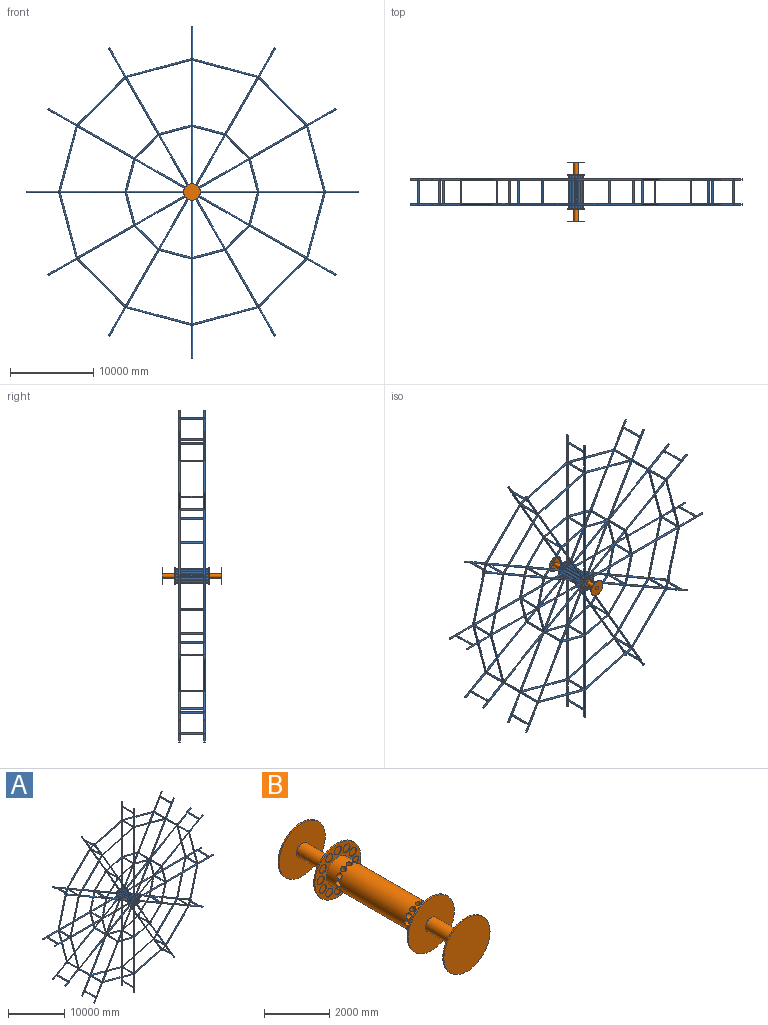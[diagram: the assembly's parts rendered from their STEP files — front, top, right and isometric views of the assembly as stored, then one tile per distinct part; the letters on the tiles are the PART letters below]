
ASSEMBLY  parts=2 mates=1
PART A: 240 faces, bbox 40000x4040x40000 mm
  f0: cylinder r=100mm len=7138.2mm, axis (1,0,0), area 4413707.7mm2, adj f8,f15,f18,f225
  f1: cylinder r=100mm len=8000mm, axis (1,0,0), area 4927074.2mm2, adj f15,f16,f18,f19,f218,f225
  f2: cylinder r=100mm len=638.2mm, axis (1,0,0), area 239270.4mm2, adj f8,f89,f217
  f3: cylinder r=100mm len=8000mm, axis (1,0,0), area 4927074.2mm2, adj f6,f7,f15,f16,f223,f224
  f4: cylinder r=100mm len=7138.2mm, axis (1,0,0), area 4413701.9mm2, adj f6,f8,f15,f224
  f5: cylinder r=100mm len=638.2mm, axis (1,0,0), area 239279.2mm2, adj f8,f95,f216
  f6: cylinder r=100mm len=4051.76mm, axis (-0.26,0,0.97), area 2502458.8mm2, adj f3,f4,f15,f206,f207,f222
  f7: cylinder r=100mm len=8051.76mm, axis (-0.26,0,0.97), area 5104391.6mm2, adj f3,f14,f16,f205,f221,f222
  f8: cylinder r=150mm len=4040mm, axis (0,1,0), area 3673361.7mm2, adj f0,f2,f4,f5,f9,f10
  f9: plane 300x300mm, normal (0,-1,0), area 70685.8mm2, adj f8
  f10: plane 300x300mm, normal (0,1,0), area 70685.8mm2, adj f8
  f11: plane 200x200mm, normal (1,0,0), area 31415.9mm2, adj f12
  f12: cylinder r=100mm len=4000mm, axis (1,0,0), area 2432718.2mm2, adj f11,f16,f17,f19,f218
  f13: plane 200x200mm, normal (1,0,0), area 31415.9mm2, adj f14
  f14: cylinder r=100mm len=4000mm, axis (1,0,0), area 2432718.2mm2, adj f7,f13,f16,f17,f223
  f15: cylinder r=100mm len=2878.25mm, axis (0,1,0), area 1772786.4mm2, adj f0,f1,f3,f4,f6,f18,f224,f225
  f16: cylinder r=100mm len=2878.25mm, axis (0,1,0), area 1772786.4mm2, adj f1,f3,f7,f12,f14,f19,f218,f223
  f17: cylinder r=100mm len=3000mm, axis (0,1,0), area 1804955.6mm2, adj f12,f14
  f18: cylinder r=100mm len=4051.76mm, axis (-0.26,0,0.97), area 2502458.8mm2, adj f0,f1,f15,f206,f209,f220
  f19: cylinder r=100mm len=8051.76mm, axis (-0.26,0,0.97), area 5104391.6mm2, adj f1,f12,f16,f205,f219,f220
  f20: cylinder r=100mm len=652.7mm, axis (0.87,0,0.5), area 239274.4mm2, adj f24,f201,f239
  f21: plane 200x173.21mm, normal (-0.87,0,-0.5), area 31415.9mm2, adj f28
  f22: plane 200x173.21mm, normal (-0.87,0,-0.5), area 31415.9mm2, adj f31
  f23: cylinder r=100mm len=3000mm, axis (0,1,0), area 1804955.6mm2, adj f28,f31
  f24: cylinder r=150mm len=4040mm, axis (0,1,0), area 3673404.8mm2, adj f20,f25,f26,f27,f30,f32
  f25: plane 300x300mm, normal (0,-1,0), area 70685.8mm2, adj f24
  f26: plane 300x300mm, normal (0,1,0), area 70685.8mm2, adj f24
  f27: cylinder r=100mm len=652.7mm, axis (0.87,0,0.5), area 239269.5mm2, adj f24,f194,f234
  f28: cylinder r=100mm len=3564.1mm, axis (0.87,0,0.5), area 2432718.2mm2, adj f21,f23,f107,f128,f130
  f29: cylinder r=100mm len=7028.2mm, axis (0.87,0,0.5), area 4927074.2mm2, adj f106,f107,f128,f129,f130,f131
  f30: cylinder r=100mm len=6281.86mm, axis (0.87,0,0.5), area 4413703.6mm2, adj f24,f106,f129,f131
  f31: cylinder r=100mm len=3564.1mm, axis (0.87,0,0.5), area 2432718.2mm2, adj f22,f23,f103,f130,f132
  f32: cylinder r=100mm len=6281.86mm, axis (0.87,0,0.5), area 4413706.1mm2, adj f24,f102,f131,f133
  f33: cylinder r=100mm len=7028.2mm, axis (0.87,0,0.5), area 4927074.2mm2, adj f102,f103,f130,f131,f132,f133
  f34: cylinder r=100mm len=7028.2mm, axis (0.5,0,0.87), area 4927074.2mm2, adj f40,f41,f49,f50,f214,f215
  f35: cylinder r=100mm len=3564.1mm, axis (0.5,0,0.87), area 2432718.2mm2, adj f41,f47,f50,f51,f214
  f36: cylinder r=100mm len=7028.2mm, axis (0.5,0,0.87), area 4927074.2mm2, adj f49,f50,f52,f53,f202,f203
  f37: cylinder r=100mm len=3564.1mm, axis (0.5,0,0.87), area 2432718.2mm2, adj f45,f50,f51,f53,f202
  f38: cylinder r=100mm len=652.7mm, axis (0.5,0,0.87), area 239270.4mm2, adj f42,f183,f217
  f39: cylinder r=100mm len=652.7mm, axis (0.5,0,0.87), area 239279.2mm2, adj f42,f182,f216
  f40: cylinder r=100mm len=4051.76mm, axis (-0.97,0,0.26), area 2502458.8mm2, adj f34,f48,f49,f172,f173,f187
  f41: cylinder r=100mm len=8051.76mm, axis (-0.97,0,0.26), area 5104391.6mm2, adj f34,f35,f50,f171,f186,f187
  f42: cylinder r=150mm len=4040mm, axis (0,1,0), area 3673361.7mm2, adj f38,f39,f43,f44,f46,f48
  f43: plane 300x300mm, normal (0,-1,0), area 70685.8mm2, adj f42
  f44: plane 300x300mm, normal (0,1,0), area 70685.8mm2, adj f42
  f45: plane 200x173.21mm, normal (0.5,0,0.87), area 31415.9mm2, adj f37
  f46: cylinder r=100mm len=6281.86mm, axis (0.5,0,0.87), area 4413707.7mm2, adj f42,f49,f52,f203
  f47: plane 200x173.21mm, normal (0.5,0,0.87), area 31415.9mm2, adj f35
  f48: cylinder r=100mm len=6281.86mm, axis (0.5,0,0.87), area 4413701.9mm2, adj f40,f42,f49,f215
  f49: cylinder r=100mm len=2878.25mm, axis (0,1,0), area 1772786.4mm2, adj f34,f36,f40,f46,f48,f52,f203,f215
  f50: cylinder r=100mm len=2878.25mm, axis (0,1,0), area 1772786.4mm2, adj f34,f35,f36,f37,f41,f53,f202,f214
  f51: cylinder r=100mm len=3000mm, axis (0,1,0), area 1804955.6mm2, adj f35,f37
  f52: cylinder r=100mm len=4051.76mm, axis (-0.97,0,0.26), area 2502458.8mm2, adj f36,f46,f49,f172,f175,f185
  f53: cylinder r=100mm len=8051.76mm, axis (-0.97,0,0.26), area 5104391.6mm2, adj f36,f37,f50,f171,f184,f185
  f54: cylinder r=100mm len=638.2mm, axis (0,0,1), area 239274.4mm2, adj f58,f167,f201
  f55: plane 200x200mm, normal (0,0,-1), area 31415.9mm2, adj f62
  f56: plane 200x200mm, normal (0,0,-1), area 31415.9mm2, adj f65
  f57: cylinder r=100mm len=3000mm, axis (0,1,0), area 1804955.6mm2, adj f62,f65
  f58: cylinder r=150mm len=4040mm, axis (0,1,0), area 3673404.8mm2, adj f54,f59,f60,f61,f64,f66
  f59: plane 300x300mm, normal (0,-1,0), area 70685.8mm2, adj f58
  f60: plane 300x300mm, normal (0,1,0), area 70685.8mm2, adj f58
  f61: cylinder r=100mm len=638.2mm, axis (0,0,1), area 239269.5mm2, adj f58,f160,f194
  f62: cylinder r=100mm len=4000mm, axis (0,0,1), area 2432718.2mm2, adj f55,f57,f113,f122,f124
  f63: cylinder r=100mm len=8000mm, axis (0,0,1), area 4927074.2mm2, adj f112,f113,f122,f123,f124,f125
  f64: cylinder r=100mm len=7138.2mm, axis (0,0,1), area 4413703.6mm2, adj f58,f112,f123,f125
  f65: cylinder r=100mm len=4000mm, axis (0,0,1), area 2432718.2mm2, adj f56,f57,f109,f124,f126
  f66: cylinder r=100mm len=7138.2mm, axis (0,0,1), area 4413706.1mm2, adj f58,f108,f125,f127
  f67: cylinder r=100mm len=8000mm, axis (0,0,1), area 4927074.2mm2, adj f108,f109,f124,f125,f126,f127
  f68: cylinder r=100mm len=7028.2mm, axis (-0.5,0,0.87), area 4927074.2mm2, adj f74,f75,f83,f84,f180,f181
  f69: cylinder r=100mm len=3564.1mm, axis (-0.5,0,0.87), area 2432718.2mm2, adj f75,f81,f84,f85,f180
  f70: cylinder r=100mm len=7028.2mm, axis (-0.5,0,0.87), area 4927074.2mm2, adj f83,f84,f86,f87,f168,f169
  f71: cylinder r=100mm len=3564.1mm, axis (-0.5,0,0.87), area 2432718.2mm2, adj f79,f84,f85,f87,f168
  f72: cylinder r=100mm len=652.7mm, axis (-0.5,0,0.87), area 239270.4mm2, adj f76,f149,f183
  f73: cylinder r=100mm len=652.7mm, axis (-0.5,0,0.87), area 239279.2mm2, adj f76,f148,f182
  f74: cylinder r=100mm len=3069.62mm, axis (-0.71,0,-0.71), area 2502458.8mm2, adj f68,f82,f83,f138,f139,f153
  f75: cylinder r=100mm len=5997.83mm, axis (-0.71,0,-0.71), area 5104391.6mm2, adj f68,f69,f84,f137,f152,f153
  f76: cylinder r=150mm len=4040mm, axis (0,1,0), area 3673361.7mm2, adj f72,f73,f77,f78,f80,f82
  f77: plane 300x300mm, normal (0,-1,0), area 70685.8mm2, adj f76
  f78: plane 300x300mm, normal (0,1,0), area 70685.8mm2, adj f76
  f79: plane 200x173.21mm, normal (-0.5,0,0.87), area 31415.9mm2, adj f71
  f80: cylinder r=100mm len=6281.86mm, axis (-0.5,0,0.87), area 4413707.7mm2, adj f76,f83,f86,f169
  f81: plane 200x173.21mm, normal (-0.5,0,0.87), area 31415.9mm2, adj f69
  f82: cylinder r=100mm len=6281.86mm, axis (-0.5,0,0.87), area 4413701.9mm2, adj f74,f76,f83,f181
  f83: cylinder r=100mm len=2878.25mm, axis (0,1,0), area 1772786.4mm2, adj f68,f70,f74,f80,f82,f86,f169,f181
  f84: cylinder r=100mm len=2878.25mm, axis (0,1,0), area 1772786.4mm2, adj f68,f69,f70,f71,f75,f87,f168,f180
  f85: cylinder r=100mm len=3000mm, axis (0,1,0), area 1804955.6mm2, adj f69,f71
  f86: cylinder r=100mm len=3069.62mm, axis (-0.71,0,-0.71), area 2502458.8mm2, adj f70,f80,f83,f138,f141,f151
  f87: cylinder r=100mm len=5997.83mm, axis (-0.71,0,-0.71), area 5104391.6mm2, adj f70,f71,f84,f137,f150,f151
  f88: plane 200x173.21mm, normal (0.87,0,-0.5), area 31415.9mm2, adj f96
  f89: cylinder r=100mm len=652.69mm, axis (-0.87,0,0.5), area 239271.8mm2, adj f2,f92,f167
  f90: plane 200x173.21mm, normal (0.87,0,-0.5), area 31415.9mm2, adj f99
  f91: cylinder r=100mm len=3000mm, axis (0,1,0), area 1804955.6mm2, adj f96,f99
  f92: cylinder r=150mm len=4040mm, axis (0,1,0), area 3673443.3mm2, adj f89,f93,f94,f95,f98,f100
  f93: plane 300x300mm, normal (0,-1,0), area 70685.8mm2, adj f92
  f94: plane 300x300mm, normal (0,1,0), area 70685.8mm2, adj f92
  f95: cylinder r=100mm len=652.69mm, axis (-0.87,0,0.5), area 239270.8mm2, adj f5,f92,f160
  f96: cylinder r=100mm len=3564.1mm, axis (-0.87,0,0.5), area 2432718.2mm2, adj f88,f91,f119,f120,f218
  f97: cylinder r=100mm len=7028.2mm, axis (-0.87,0,0.5), area 4927074.2mm2, adj f118,f119,f120,f121,f218,f225
  f98: cylinder r=100mm len=6281.86mm, axis (-0.87,0,0.5), area 4413703.6mm2, adj f92,f118,f121,f225
  f99: cylinder r=100mm len=3564.1mm, axis (-0.87,0,0.5), area 2432718.2mm2, adj f90,f91,f115,f120,f223
  f100: cylinder r=100mm len=6281.86mm, axis (-0.87,0,0.5), area 4413706.1mm2, adj f92,f114,f121,f224
  f101: cylinder r=100mm len=7028.2mm, axis (-0.87,0,0.5), area 4927074.2mm2, adj f114,f115,f120,f121,f223,f224
  f102: cylinder r=100mm len=4051.76mm, axis (0.26,0,-0.97), area 2502458.8mm2, adj f32,f33,f104,f131,f226,f227
  f103: cylinder r=100mm len=8051.76mm, axis (0.26,0,-0.97), area 5104391.6mm2, adj f31,f33,f105,f130,f226,f228
  f104: cylinder r=100mm len=2878.25mm, axis (0,1,0), area 1772786.4mm2, adj f102,f106,f135,f147,f226,f227,f229,f230
  f105: cylinder r=100mm len=2878.25mm, axis (0,1,0), area 1772786.4mm2, adj f103,f107,f134,f146,f226,f228,f230,f231
  f106: cylinder r=100mm len=4051.76mm, axis (0.26,0,-0.97), area 2502458.8mm2, adj f29,f30,f104,f131,f229,f230
  f107: cylinder r=100mm len=8051.76mm, axis (0.26,0,-0.97), area 5104391.6mm2, adj f28,f29,f105,f130,f230,f231
  f108: cylinder r=100mm len=4051.76mm, axis (0.97,0,-0.26), area 2502458.8mm2, adj f66,f67,f110,f125,f188,f189
  f109: cylinder r=100mm len=8051.76mm, axis (0.97,0,-0.26), area 5104391.6mm2, adj f65,f67,f111,f124,f188,f190
  f110: cylinder r=100mm len=2878.25mm, axis (0,1,0), area 1772786.4mm2, adj f108,f112,f129,f133,f188,f189,f191,f192
  f111: cylinder r=100mm len=2878.25mm, axis (0,1,0), area 1772786.4mm2, adj f109,f113,f128,f132,f188,f190,f192,f193
  f112: cylinder r=100mm len=4051.76mm, axis (0.97,0,-0.26), area 2502458.8mm2, adj f63,f64,f110,f125,f191,f192
  f113: cylinder r=100mm len=8051.76mm, axis (0.97,0,-0.26), area 5104391.6mm2, adj f62,f63,f111,f124,f192,f193
  f114: cylinder r=100mm len=3069.62mm, axis (0.71,0,0.71), area 2502458.8mm2, adj f100,f101,f116,f121,f154,f155
  f115: cylinder r=100mm len=5997.83mm, axis (0.71,0,0.71), area 5104391.6mm2, adj f99,f101,f117,f120,f154,f156
  f116: cylinder r=100mm len=2878.25mm, axis (0,1,0), area 1772786.4mm2, adj f114,f118,f123,f127,f154,f155,f157,f158
  f117: cylinder r=100mm len=2878.25mm, axis (0,1,0), area 1772786.4mm2, adj f115,f119,f122,f126,f154,f156,f158,f159
  f118: cylinder r=100mm len=3069.62mm, axis (0.71,0,0.71), area 2502458.8mm2, adj f97,f98,f116,f121,f157,f158
  f119: cylinder r=100mm len=5997.83mm, axis (0.71,0,0.71), area 5104391.6mm2, adj f96,f97,f117,f120,f158,f159
  f120: cylinder r=100mm len=2878.25mm, axis (0,1,0), area 1772786.4mm2, adj f96,f97,f99,f101,f115,f119,f218,f223
  f121: cylinder r=100mm len=2878.25mm, axis (0,1,0), area 1772786.4mm2, adj f97,f98,f100,f101,f114,f118,f224,f225
  f122: cylinder r=100mm len=8051.76mm, axis (0.97,0,0.26), area 5104391.6mm2, adj f62,f63,f117,f124,f158,f159
  f123: cylinder r=100mm len=4051.76mm, axis (0.97,0,0.26), area 2502458.8mm2, adj f63,f64,f116,f125,f157,f158
  f124: cylinder r=100mm len=2878.25mm, axis (0,1,0), area 1772786.4mm2, adj f62,f63,f65,f67,f109,f113,f122,f126
  f125: cylinder r=100mm len=2878.25mm, axis (0,1,0), area 1772786.4mm2, adj f63,f64,f66,f67,f108,f112,f123,f127
  f126: cylinder r=100mm len=8051.76mm, axis (0.97,0,0.26), area 5104391.6mm2, adj f65,f67,f117,f124,f154,f156
  f127: cylinder r=100mm len=4051.76mm, axis (0.97,0,0.26), area 2502458.8mm2, adj f66,f67,f116,f125,f154,f155
  f128: cylinder r=100mm len=5997.83mm, axis (0.71,0,-0.71), area 5104391.6mm2, adj f28,f29,f111,f130,f192,f193
  f129: cylinder r=100mm len=3069.62mm, axis (0.71,0,-0.71), area 2502458.8mm2, adj f29,f30,f110,f131,f191,f192
  f130: cylinder r=100mm len=2878.25mm, axis (0,1,0), area 1772786.4mm2, adj f28,f29,f31,f33,f103,f107,f128,f132
  f131: cylinder r=100mm len=2878.25mm, axis (0,1,0), area 1772786.4mm2, adj f29,f30,f32,f33,f102,f106,f129,f133
  f132: cylinder r=100mm len=5997.83mm, axis (0.71,0,-0.71), area 5104391.6mm2, adj f31,f33,f111,f130,f188,f190
  f133: cylinder r=100mm len=3069.62mm, axis (0.71,0,-0.71), area 2502458.8mm2, adj f32,f33,f110,f131,f188,f189
  f134: cylinder r=100mm len=8051.76mm, axis (-0.26,0,-0.97), area 5104391.6mm2, adj f105,f137,f150,f151,f230,f231
  f135: cylinder r=100mm len=4051.76mm, axis (-0.26,0,-0.97), area 2502458.8mm2, adj f104,f138,f141,f151,f229,f230
  f136: cylinder r=100mm len=3000mm, axis (0,1,0), area 1804955.6mm2, adj f150,f152
  f137: cylinder r=100mm len=2878.25mm, axis (0,1,0), area 1772786.4mm2, adj f75,f87,f134,f146,f150,f151,f152,f153
  f138: cylinder r=100mm len=2878.25mm, axis (0,1,0), area 1772786.4mm2, adj f74,f86,f135,f139,f141,f147,f151,f153
  f139: cylinder r=100mm len=6281.86mm, axis (-0.87,0,0.5), area 4413701.9mm2, adj f74,f138,f145,f147
  f140: plane 200x173.21mm, normal (-0.87,0,0.5), area 31415.9mm2, adj f152
  f141: cylinder r=100mm len=6281.86mm, axis (-0.87,0,0.5), area 4413707.7mm2, adj f86,f135,f138,f145
  f142: plane 200x173.21mm, normal (-0.87,0,0.5), area 31415.9mm2, adj f150
  f143: plane 300x300mm, normal (0,1,0), area 70685.8mm2, adj f145
  f144: plane 300x300mm, normal (0,-1,0), area 70685.8mm2, adj f145
  f145: cylinder r=150mm len=4040mm, axis (0,1,0), area 3673361.7mm2, adj f139,f141,f143,f144,f148,f149
  f146: cylinder r=100mm len=8051.76mm, axis (-0.26,0,-0.97), area 5104391.6mm2, adj f105,f137,f152,f153,f226,f228
  f147: cylinder r=100mm len=4051.76mm, axis (-0.26,0,-0.97), area 2502458.8mm2, adj f104,f138,f139,f153,f226,f227
  f148: cylinder r=100mm len=652.7mm, axis (-0.87,0,0.5), area 239279.3mm2, adj f73,f145,f234
  f149: cylinder r=100mm len=652.7mm, axis (-0.87,0,0.5), area 239270.5mm2, adj f72,f145,f239
  f150: cylinder r=100mm len=3564.1mm, axis (-0.87,0,0.5), area 2432718.2mm2, adj f87,f134,f136,f137,f142
  f151: cylinder r=100mm len=7028.2mm, axis (-0.87,0,0.5), area 4927074.2mm2, adj f86,f87,f134,f135,f137,f138
  f152: cylinder r=100mm len=3564.1mm, axis (-0.87,0,0.5), area 2432718.2mm2, adj f75,f136,f137,f140,f146
  f153: cylinder r=100mm len=7028.2mm, axis (-0.87,0,0.5), area 4927074.2mm2, adj f74,f75,f137,f138,f146,f147
  f154: cylinder r=100mm len=7028.2mm, axis (-0.5,0,0.87), area 4927074.2mm2, adj f114,f115,f116,f117,f126,f127
  f155: cylinder r=100mm len=6281.86mm, axis (-0.5,0,0.87), area 4413706.1mm2, adj f114,f116,f127,f163
  f156: cylinder r=100mm len=3564.1mm, axis (-0.5,0,0.87), area 2432718.2mm2, adj f115,f117,f126,f164,f165
  f157: cylinder r=100mm len=6281.86mm, axis (-0.5,0,0.87), area 4413703.6mm2, adj f116,f118,f123,f163
  f158: cylinder r=100mm len=7028.2mm, axis (-0.5,0,0.87), area 4927074.2mm2, adj f116,f117,f118,f119,f122,f123
  f159: cylinder r=100mm len=3564.1mm, axis (-0.5,0,0.87), area 2432718.2mm2, adj f117,f119,f122,f164,f166
  f160: cylinder r=100mm len=652.7mm, axis (-0.5,0,0.87), area 239262.5mm2, adj f61,f95,f163
  f161: plane 300x300mm, normal (0,1,0), area 70685.8mm2, adj f163
  f162: plane 300x300mm, normal (0,-1,0), area 70685.8mm2, adj f163
  f163: cylinder r=150mm len=4040mm, axis (0,1,0), area 3673404.8mm2, adj f155,f157,f160,f161,f162,f167
  f164: cylinder r=100mm len=3000mm, axis (0,1,0), area 1804955.6mm2, adj f156,f159
  f165: plane 200x173.21mm, normal (0.5,0,-0.87), area 31415.9mm2, adj f156
  f166: plane 200x173.21mm, normal (0.5,0,-0.87), area 31415.9mm2, adj f159
  f167: cylinder r=100mm len=652.7mm, axis (-0.5,0,0.87), area 239270.3mm2, adj f54,f89,f163
  f168: cylinder r=100mm len=8051.76mm, axis (-0.97,0,-0.26), area 5104391.6mm2, adj f70,f71,f84,f171,f184,f185
  f169: cylinder r=100mm len=4051.76mm, axis (-0.97,0,-0.26), area 2502458.8mm2, adj f70,f80,f83,f172,f175,f185
  f170: cylinder r=100mm len=3000mm, axis (0,1,0), area 1804955.6mm2, adj f184,f186
  f171: cylinder r=100mm len=2878.25mm, axis (0,1,0), area 1772786.4mm2, adj f41,f53,f168,f180,f184,f185,f186,f187
  f172: cylinder r=100mm len=2878.25mm, axis (0,1,0), area 1772786.4mm2, adj f40,f52,f169,f173,f175,f181,f185,f187
  f173: cylinder r=100mm len=7138.2mm, axis (0,0,1), area 4413701.9mm2, adj f40,f172,f179,f181
  f174: plane 200x200mm, normal (0,0,1), area 31415.9mm2, adj f186
  f175: cylinder r=100mm len=7138.2mm, axis (0,0,1), area 4413707.7mm2, adj f52,f169,f172,f179
  f176: plane 200x200mm, normal (0,0,1), area 31415.9mm2, adj f184
  f177: plane 300x300mm, normal (0,1,0), area 70685.8mm2, adj f179
  f178: plane 300x300mm, normal (0,-1,0), area 70685.8mm2, adj f179
  f179: cylinder r=150mm len=4040mm, axis (0,1,0), area 3673361.7mm2, adj f173,f175,f177,f178,f182,f183
  f180: cylinder r=100mm len=8051.76mm, axis (-0.97,0,-0.26), area 5104391.6mm2, adj f68,f69,f84,f171,f186,f187
  f181: cylinder r=100mm len=4051.76mm, axis (-0.97,0,-0.26), area 2502458.8mm2, adj f68,f82,f83,f172,f173,f187
  f182: cylinder r=100mm len=638.2mm, axis (0,0,1), area 239279.2mm2, adj f39,f73,f179
  f183: cylinder r=100mm len=638.2mm, axis (0,0,1), area 239270.4mm2, adj f38,f72,f179
  f184: cylinder r=100mm len=4000mm, axis (0,0,1), area 2432718.2mm2, adj f53,f168,f170,f171,f176
  f185: cylinder r=100mm len=8000mm, axis (0,0,1), area 4927074.2mm2, adj f52,f53,f168,f169,f171,f172
  f186: cylinder r=100mm len=4000mm, axis (0,0,1), area 2432718.2mm2, adj f41,f170,f171,f174,f180
  f187: cylinder r=100mm len=8000mm, axis (0,0,1), area 4927074.2mm2, adj f40,f41,f171,f172,f180,f181
  f188: cylinder r=100mm len=7028.2mm, axis (0.5,0,0.87), area 4927074.2mm2, adj f108,f109,f110,f111,f132,f133
  f189: cylinder r=100mm len=6281.86mm, axis (0.5,0,0.87), area 4413706.1mm2, adj f108,f110,f133,f197
  f190: cylinder r=100mm len=3564.1mm, axis (0.5,0,0.87), area 2432718.2mm2, adj f109,f111,f132,f198,f199
  f191: cylinder r=100mm len=6281.86mm, axis (0.5,0,0.87), area 4413703.6mm2, adj f110,f112,f129,f197
  f192: cylinder r=100mm len=7028.2mm, axis (0.5,0,0.87), area 4927074.2mm2, adj f110,f111,f112,f113,f128,f129
  f193: cylinder r=100mm len=3564.1mm, axis (0.5,0,0.87), area 2432718.2mm2, adj f111,f113,f128,f198,f200
  f194: cylinder r=100mm len=652.7mm, axis (0.5,0,0.87), area 239262.5mm2, adj f27,f61,f197
  f195: plane 300x300mm, normal (0,1,0), area 70685.8mm2, adj f197
  f196: plane 300x300mm, normal (0,-1,0), area 70685.8mm2, adj f197
  f197: cylinder r=150mm len=4040mm, axis (0,1,0), area 3673404.8mm2, adj f189,f191,f194,f195,f196,f201
  f198: cylinder r=100mm len=3000mm, axis (0,1,0), area 1804955.6mm2, adj f190,f193
  f199: plane 200x173.21mm, normal (-0.5,0,-0.87), area 31415.9mm2, adj f190
  f200: plane 200x173.21mm, normal (-0.5,0,-0.87), area 31415.9mm2, adj f193
  f201: cylinder r=100mm len=652.7mm, axis (0.5,0,0.87), area 239270.3mm2, adj f20,f54,f197
  f202: cylinder r=100mm len=5997.83mm, axis (-0.71,0,0.71), area 5104391.6mm2, adj f36,f37,f50,f205,f219,f220
  f203: cylinder r=100mm len=3069.62mm, axis (-0.71,0,0.71), area 2502458.8mm2, adj f36,f46,f49,f206,f209,f220
  f204: cylinder r=100mm len=3000mm, axis (0,1,0), area 1804955.6mm2, adj f219,f221
  f205: cylinder r=100mm len=2878.25mm, axis (0,1,0), area 1772786.4mm2, adj f7,f19,f202,f214,f219,f220,f221,f222
  f206: cylinder r=100mm len=2878.25mm, axis (0,1,0), area 1772786.4mm2, adj f6,f18,f203,f207,f209,f215,f220,f222
  f207: cylinder r=100mm len=6281.86mm, axis (0.87,0,0.5), area 4413701.9mm2, adj f6,f206,f213,f215
  f208: plane 200x173.21mm, normal (0.87,0,0.5), area 31415.9mm2, adj f221
  f209: cylinder r=100mm len=6281.86mm, axis (0.87,0,0.5), area 4413707.7mm2, adj f18,f203,f206,f213
  f210: plane 200x173.21mm, normal (0.87,0,0.5), area 31415.9mm2, adj f219
  f211: plane 300x300mm, normal (0,1,0), area 70685.8mm2, adj f213
  f212: plane 300x300mm, normal (0,-1,0), area 70685.8mm2, adj f213
  f213: cylinder r=150mm len=4040mm, axis (0,1,0), area 3673361.7mm2, adj f207,f209,f211,f212,f216,f217
  f214: cylinder r=100mm len=5997.83mm, axis (-0.71,0,0.71), area 5104391.6mm2, adj f34,f35,f50,f205,f221,f222
  f215: cylinder r=100mm len=3069.62mm, axis (-0.71,0,0.71), area 2502458.8mm2, adj f34,f48,f49,f206,f207,f222
  f216: cylinder r=100mm len=652.7mm, axis (0.87,0,0.5), area 239279.2mm2, adj f5,f39,f213
  f217: cylinder r=100mm len=652.7mm, axis (0.87,0,0.5), area 239270.4mm2, adj f2,f38,f213
  f218: cylinder r=100mm len=8051.76mm, axis (0.26,0,0.97), area 5104391.6mm2, adj f1,f12,f16,f96,f97,f120
  f219: cylinder r=100mm len=3564.1mm, axis (0.87,0,0.5), area 2432718.2mm2, adj f19,f202,f204,f205,f210
  f220: cylinder r=100mm len=7028.2mm, axis (0.87,0,0.5), area 4927074.2mm2, adj f18,f19,f202,f203,f205,f206
  f221: cylinder r=100mm len=3564.1mm, axis (0.87,0,0.5), area 2432718.2mm2, adj f7,f204,f205,f208,f214
  f222: cylinder r=100mm len=7028.2mm, axis (0.87,0,0.5), area 4927074.2mm2, adj f6,f7,f205,f206,f214,f215
  f223: cylinder r=100mm len=8051.76mm, axis (0.26,0,0.97), area 5104391.6mm2, adj f3,f14,f16,f99,f101,f120
  f224: cylinder r=100mm len=4051.76mm, axis (0.26,0,0.97), area 2502458.8mm2, adj f3,f4,f15,f100,f101,f121
  f225: cylinder r=100mm len=4051.76mm, axis (0.26,0,0.97), area 2502458.8mm2, adj f0,f1,f15,f97,f98,f121
  f226: cylinder r=100mm len=8000mm, axis (1,0,0), area 4927074.2mm2, adj f102,f103,f104,f105,f146,f147
  f227: cylinder r=100mm len=7138.2mm, axis (1,0,0), area 4413706.1mm2, adj f102,f104,f147,f237
  f228: cylinder r=100mm len=4000mm, axis (1,0,0), area 2432718.2mm2, adj f103,f105,f146,f232,f233
  f229: cylinder r=100mm len=7138.2mm, axis (1,0,0), area 4413703.6mm2, adj f104,f106,f135,f237
  f230: cylinder r=100mm len=8000mm, axis (1,0,0), area 4927074.2mm2, adj f104,f105,f106,f107,f134,f135
  f231: cylinder r=100mm len=4000mm, axis (1,0,0), area 2432718.2mm2, adj f105,f107,f134,f232,f238
  f232: cylinder r=100mm len=3000mm, axis (0,1,0), area 1804955.6mm2, adj f228,f231
  f233: plane 200x200mm, normal (-1,0,0), area 31415.9mm2, adj f228
  f234: cylinder r=100mm len=638.2mm, axis (1,0,0), area 239269.5mm2, adj f27,f148,f237
  f235: plane 300x300mm, normal (0,1,0), area 70685.8mm2, adj f237
  f236: plane 300x300mm, normal (0,-1,0), area 70685.8mm2, adj f237
  f237: cylinder r=150mm len=4040mm, axis (0,1,0), area 3673404.8mm2, adj f227,f229,f234,f235,f236,f239
  f238: plane 200x200mm, normal (-1,0,0), area 31415.9mm2, adj f231
  f239: cylinder r=100mm len=638.2mm, axis (1,0,0), area 239274.4mm2, adj f20,f149,f237
PART B: 87 faces, bbox 2000x7200x2000 mm
  f0: cylinder r=500mm len=4000mm, axis (0,1,0), area 11808607.6mm2, adj f3,f6,f55,f56,f57,f58,f59,f60
  f1: cylinder r=1000mm len=2000mm, axis (0,1,0), area 314159.3mm2, adj f2,f3
  f2: plane 2000x2000mm, normal (0,-1,0), area 2945243.1mm2, adj f1,f79
  f3: plane 2000x2000mm, normal (0,1,0), area 1507964.5mm2, adj f0,f1,f32,f34,f36,f38,f40,f42
  f4: cylinder r=1000mm len=2000mm, axis (0,-1,0), area 314159.3mm2, adj f5,f6
  f5: plane 2000x2000mm, normal (0,1,0), area 2945243.1mm2, adj f4,f83
  f6: plane 2000x2000mm, normal (0,-1,0), area 1507964.5mm2, adj f0,f4,f8,f10,f12,f14,f16,f18
  f7: plane 300x300mm, normal (0,-1,0), area 70685.8mm2, adj f8
  f8: cylinder r=150mm len=300mm, axis (0,1,0), area 18849.6mm2, adj f6,f7
  f9: plane 300x300mm, normal (0,-1,0), area 70685.8mm2, adj f10
  f10: cylinder r=150mm len=300mm, axis (0,1,0), area 18849.6mm2, adj f6,f9
  f11: plane 300x300mm, normal (0,-1,0), area 70685.8mm2, adj f12
  f12: cylinder r=150mm len=300mm, axis (0,1,0), area 18849.6mm2, adj f6,f11
  f13: plane 300x300mm, normal (0,-1,0), area 70685.8mm2, adj f14
  f14: cylinder r=150mm len=300mm, axis (0,1,0), area 18849.6mm2, adj f6,f13
  f15: plane 300x300mm, normal (0,-1,0), area 70685.8mm2, adj f16
  f16: cylinder r=150mm len=300mm, axis (0,1,0), area 18849.6mm2, adj f6,f15
  f17: plane 300x300mm, normal (0,-1,0), area 70685.8mm2, adj f18
  f18: cylinder r=150mm len=300mm, axis (0,1,0), area 18849.6mm2, adj f6,f17
  f19: plane 300x300mm, normal (0,-1,0), area 70685.8mm2, adj f20
  f20: cylinder r=150mm len=300mm, axis (0,1,0), area 18849.6mm2, adj f6,f19
  f21: plane 300x300mm, normal (0,-1,0), area 70685.8mm2, adj f22
  f22: cylinder r=150mm len=300mm, axis (0,1,0), area 18849.6mm2, adj f6,f21
  f23: plane 300x300mm, normal (0,-1,0), area 70685.8mm2, adj f24
  f24: cylinder r=150mm len=300mm, axis (0,1,0), area 18849.6mm2, adj f6,f23
  f25: plane 300x300mm, normal (0,-1,0), area 70685.8mm2, adj f26
  f26: cylinder r=150mm len=300mm, axis (0,1,0), area 18849.6mm2, adj f6,f25
  f27: plane 300x300mm, normal (0,-1,0), area 70685.8mm2, adj f28
  f28: cylinder r=150mm len=300mm, axis (0,1,0), area 18849.6mm2, adj f6,f27
  f29: plane 300x300mm, normal (0,-1,0), area 70685.8mm2, adj f30
  f30: cylinder r=150mm len=300mm, axis (0,1,0), area 18849.6mm2, adj f6,f29
  f31: plane 300x300mm, normal (0,1,0), area 70685.8mm2, adj f32
  f32: cylinder r=150mm len=300mm, axis (0,1,0), area 18849.6mm2, adj f3,f31
  f33: plane 300x300mm, normal (0,1,0), area 70685.8mm2, adj f34
  f34: cylinder r=150mm len=300mm, axis (0,1,0), area 18849.6mm2, adj f3,f33
  f35: plane 300x300mm, normal (0,1,0), area 70685.8mm2, adj f36
  f36: cylinder r=150mm len=300mm, axis (0,1,0), area 18849.6mm2, adj f3,f35
  f37: plane 300x300mm, normal (0,1,0), area 70685.8mm2, adj f38
  f38: cylinder r=150mm len=300mm, axis (0,1,0), area 18849.6mm2, adj f3,f37
  f39: plane 300x300mm, normal (0,1,0), area 70685.8mm2, adj f40
  f40: cylinder r=150mm len=300mm, axis (0,1,0), area 18849.6mm2, adj f3,f39
  f41: plane 300x300mm, normal (0,1,0), area 70685.8mm2, adj f42
  f42: cylinder r=150mm len=300mm, axis (0,1,0), area 18849.6mm2, adj f3,f41
  f43: plane 300x300mm, normal (0,1,0), area 70685.8mm2, adj f44
  f44: cylinder r=150mm len=300mm, axis (0,1,0), area 18849.6mm2, adj f3,f43
  f45: plane 300x300mm, normal (0,1,0), area 70685.8mm2, adj f46
  f46: cylinder r=150mm len=300mm, axis (0,1,0), area 18849.6mm2, adj f3,f45
  f47: plane 300x300mm, normal (0,1,0), area 70685.8mm2, adj f48
  f48: cylinder r=150mm len=300mm, axis (0,1,0), area 18849.6mm2, adj f3,f47
  f49: plane 300x300mm, normal (0,1,0), area 70685.8mm2, adj f50
  f50: cylinder r=150mm len=300mm, axis (0,1,0), area 18849.6mm2, adj f3,f49
  f51: plane 300x300mm, normal (0,1,0), area 70685.8mm2, adj f52
  f52: cylinder r=150mm len=300mm, axis (0,1,0), area 18849.6mm2, adj f3,f51
  f53: plane 300x300mm, normal (0,1,0), area 70685.8mm2, adj f54
  f54: cylinder r=150mm len=300mm, axis (0,1,0), area 18849.6mm2, adj f3,f53
  f55: cylinder r=100mm len=533.01mm, axis (0.87,0,0.5), area 161707.1mm2, adj f0,f60,f66
  f56: cylinder r=100mm len=500mm, axis (0,0,1), area 161716.3mm2, adj f0,f59,f60
  f57: cylinder r=100mm len=500mm, axis (1,0,0), area 161714.9mm2, adj f0,f58,f65
  f58: cylinder r=100mm len=533.01mm, axis (-0.87,0,0.5), area 161707.1mm2, adj f0,f57,f59
  f59: cylinder r=100mm len=533.01mm, axis (-0.5,0,0.87), area 161707.1mm2, adj f0,f56,f58
  f60: cylinder r=100mm len=533.01mm, axis (0.5,0,0.87), area 161707.1mm2, adj f0,f55,f56
  f61: cylinder r=100mm len=533.01mm, axis (0.5,0,0.87), area 161714.8mm2, adj f0,f64,f65
  f62: cylinder r=100mm len=533.01mm, axis (-0.5,0,0.87), area 161714.8mm2, adj f0,f63,f64
  f63: cylinder r=100mm len=533.01mm, axis (-0.87,0,0.5), area 161714.8mm2, adj f0,f62,f66
  f64: cylinder r=100mm len=500mm, axis (0,0,1), area 161714.8mm2, adj f0,f61,f62
  f65: cylinder r=100mm len=533.01mm, axis (0.87,0,0.5), area 161714.8mm2, adj f0,f57,f61
  f66: cylinder r=100mm len=500mm, axis (1,0,0), area 161711.9mm2, adj f0,f55,f63
  f67: cylinder r=100mm len=500mm, axis (1,0,0), area 161711.6mm2, adj f0,f72,f77
  f68: cylinder r=100mm len=533.01mm, axis (0.87,0,0.5), area 161707.1mm2, adj f0,f76,f78
  f69: cylinder r=100mm len=533.01mm, axis (0.5,0,0.87), area 161714.9mm2, adj f0,f75,f77
  f70: cylinder r=100mm len=500mm, axis (0,0,1), area 161707.1mm2, adj f0,f74,f76
  f71: cylinder r=100mm len=533.01mm, axis (-0.5,0,0.87), area 161714.8mm2, adj f0,f73,f75
  f72: cylinder r=100mm len=533.01mm, axis (-0.87,0,0.5), area 161707.1mm2, adj f0,f67,f74
  f73: cylinder r=100mm len=533.01mm, axis (-0.87,0,0.5), area 161714.9mm2, adj f0,f71,f78
  f74: cylinder r=100mm len=533.01mm, axis (-0.5,0,0.87), area 161707.1mm2, adj f0,f70,f72
  f75: cylinder r=100mm len=500mm, axis (0,0,1), area 161708.6mm2, adj f0,f69,f71
  f76: cylinder r=100mm len=533.01mm, axis (0.5,0,0.87), area 161707.1mm2, adj f0,f68,f70
  f77: cylinder r=100mm len=533.01mm, axis (0.87,0,0.5), area 161714.8mm2, adj f0,f67,f69
  f78: cylinder r=100mm len=500mm, axis (1,0,0), area 161707.1mm2, adj f0,f68,f73
  f79: cylinder r=250mm len=1500mm, axis (0,1,0), area 2356194.5mm2, adj f2,f82
  f80: cylinder r=1000mm len=2000mm, axis (0,1,0), area 314159.3mm2, adj f81,f82
  f81: plane 2000x2000mm, normal (0,-1,0), area 3141592.7mm2, adj f80
  f82: plane 2000x2000mm, normal (0,1,0), area 2945243.1mm2, adj f79,f80
  f83: cylinder r=250mm len=1500mm, axis (0,-1,0), area 2356194.5mm2, adj f5,f86
  f84: cylinder r=1000mm len=2000mm, axis (0,-1,0), area 314159.3mm2, adj f85,f86
  f85: plane 2000x2000mm, normal (0,1,0), area 3141592.7mm2, adj f84
  f86: plane 2000x2000mm, normal (0,-1,0), area 2945243.1mm2, adj f83,f84
PLACE A at identity fixed
PLACE B at identity
MATE fastened A.f179 <-> B.f14  axis (0,-1,0) through (0,-2020,750)mm
